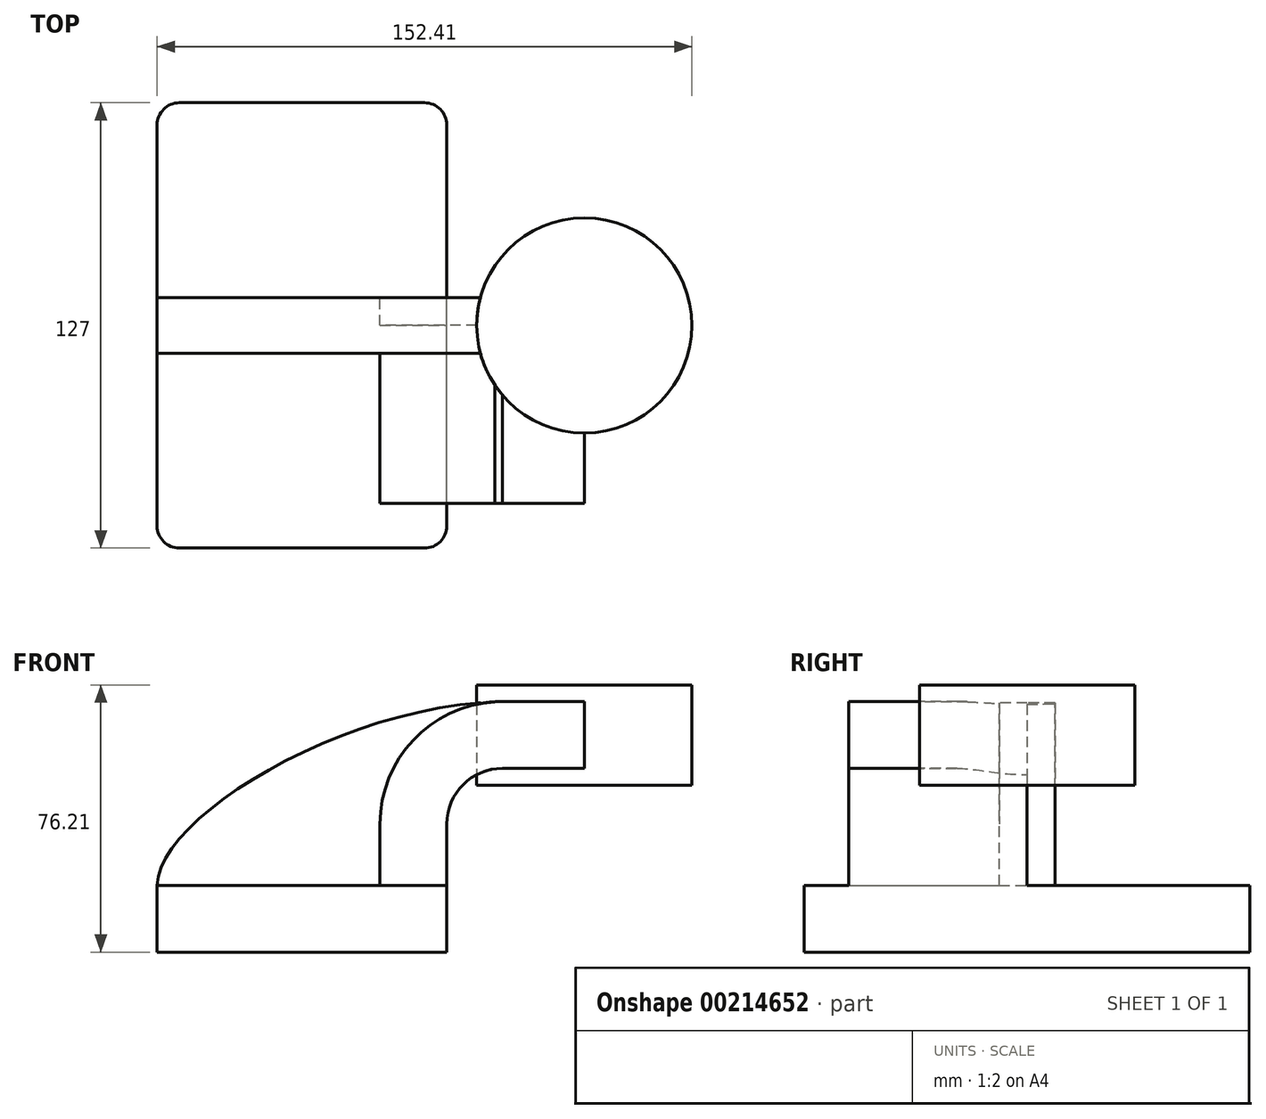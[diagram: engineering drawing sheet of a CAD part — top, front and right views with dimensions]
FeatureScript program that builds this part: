
annotation { "Feature Type Name" : "Feature", "Feature Type Description" : "" }
export const myFeature = defineFeature(function(context is Context, id is Id, definition is map)
    precondition{}
    {
        {
            var Q0;
            Q0=qCreatedBy(makeId("Front.planeOp"),FACE);
            var sketch = newSketch(context, id + "F0", { "sketchPlane" : qUnion([Q0])});
            skLineSegment(sketch, "E0.bottom", {"start": v(-41.28, -9.53) * mm, "end": v(41.28, -9.53) * mm});
            skLineSegment(sketch, "E0.top", {"start": v(-41.28, 9.53) * mm, "end": v(41.28, 9.53) * mm});
            skLineSegment(sketch, "E0.left", {"start": v(-41.28, -9.53) * mm, "end": v(-41.28, 9.53) * mm});
            skLineSegment(sketch, "E0.right", {"start": v(41.28, -9.53) * mm, "end": v(41.28, 9.53) * mm});
            skPoint(sketch, "E0.middle", {"position": v(0, 0) * mm});
            skLineSegment(sketch, "E1.bottom", {"start": v(60.32, 38.1) * mm, "end": v(111.12, 38.1) * mm});
            skLineSegment(sketch, "E1.top", {"start": v(60.32, 66.67) * mm, "end": v(111.12, 66.67) * mm});
            skLineSegment(sketch, "E1.left", {"start": v(60.32, 38.1) * mm, "end": v(60.32, 66.67) * mm});
            skLineSegment(sketch, "E1.right", {"start": v(111.12, 38.1) * mm, "end": v(111.12, 66.67) * mm});
            skPoint(sketch, "E1.middle", {"position": v(85.72, 52.39) * mm});
            skLineSegment(sketch, "E2", {"start": v(41.28, 9.53) * mm, "end": v(41.28, 27) * mm});
            skArc(sketch, "E3", {"start": v(41.27, 27) * mm, "mid": v(45.92, 38.23) * mm, "end": v(57.15, 42.88) * mm});
            skLineSegment(sketch, "E4", {"start": v(57.15, 42.88) * mm, "end": v(80.46, 42.88) * mm});
            skLineSegment(sketch, "E5.0", {"start": v(57.15, 61.93) * mm, "end": v(80.46, 61.93) * mm});
            skArc(sketch, "E5.1", {"start": v(22.22, 27) * mm, "mid": v(32.45, 51.7) * mm, "end": v(57.15, 61.93) * mm});
            skLineSegment(sketch, "E5.2", {"start": v(22.22, 9.53) * mm, "end": v(22.22, 27) * mm});
            skLineSegment(sketch, "E6", {"start": v(80.46, 38.1) * mm, "end": v(80.46, 66.67) * mm});
            skFitSpline(sketch, "E7", {"points": [v(-41.28, 9.52) * mm, v(57.15, 61.93) * mm], "startDerivative": vector(0.94, 57.52) * mm, "endDerivative": vector(138.38, 2.96) * mm});
            skSolve(sketch);
        }
        {
            var Q0;
            Q0=makeQuery(id+"F0.imprint","IMPRINT",FACE,{"disambiguationData":[TD([[makeQuery(id+"F0.imprint","IMPRINT",EDGE,{"derivedFrom":sQuery(id+"F0.wireOp",EDGE,"E0.bottom")}),1.0]])]});
            extrude(context, id + "F1", {"entities" : qUnion([Q0]), "endBound" : BoundingType.SYMMETRIC, "depth" : 127 * mm});
        }
        {
            var Q0;
            {var subQ1=sQuery(id+"F0.wireOp",EDGE,"E2");Q0=makeQuery(id+"F0.imprint","IMPRINT",FACE,{"disambiguationData":[TD([[makeQuery(id+"F0.imprint","IMPRINT",EDGE,{"derivedFrom":subQ1}),1.0]])]});}
            var Q1;
            {var subQ0=sQuery(id+"F0.wireOp",EDGE,"E4");var subQ1=sQuery(id+"F0.wireOp",EDGE,"E1.left");var subQ2=makeQuery(id+"F0.imprint","INTERSECT",VERTEX,{"derivedFrom":[subQ1,subQ0]});Q1=makeQuery(id+"F0.imprint","IMPRINT",FACE,{"disambiguationData":[TD([[makeQuery(id+"F0.imprint","IMPRINT",EDGE,{"disambiguationData":[TD([[subQ2,-1.0]])],"derivedFrom":subQ1}),-1.0]])]});}
            extrude(context, id + "F2", {"entities" : qUnion([Q0, Q1]), "operationType" : NewBodyOperationType.ADD, "depth" : 50.8 * mm});
        }
        {
            var Q0;
            {var subQ3=sQuery(id+"F0.wireOp",EDGE,"E5.2");Q0=makeQuery(id+"F0.imprint","IMPRINT",FACE,{"disambiguationData":[TD([[makeQuery(id+"F0.imprint","IMPRINT",EDGE,{"derivedFrom":subQ3}),1.0]])]});}
            extrude(context, id + "F3", {"entities" : qUnion([Q0]), "operationType" : NewBodyOperationType.ADD, "endBound" : BoundingType.SYMMETRIC, "depth" : 15.88 * mm});
        }
        {
            var Q0;
            {var subQ0=sQuery(id+"F0.wireOp",EDGE,"E1.right");Q0=makeQuery(id+"F0.imprint","IMPRINT",FACE,{"disambiguationData":[TD([[makeQuery(id+"F0.imprint","IMPRINT",EDGE,{"derivedFrom":subQ0}),1.0]])]});}
            var Q1;
            Q1=sQuery(id+"F0.wireOp",EDGE,"E6");
            revolve(context, id + "F4", {"operationType" : NewBodyOperationType.ADD, "entities" : qUnion([Q0]), "axis" : qUnion([Q1]), "revolveType" : RevolveType.FULL});
        }
        {
            var Q0;
            Q0=makeQuery(id+"F1.opExtrude","CAP_EDGE",EDGE,{"disambiguationData":[OSD([sQuery(id+"F0.wireOp",EDGE,"E0.right")])],"isStart":false});
            var Q1;
            Q1=makeQuery(id+"F1.opExtrude","CAP_EDGE",EDGE,{"disambiguationData":[OSD([sQuery(id+"F0.wireOp",EDGE,"E0.left")])],"isStart":false});
            var Q2;
            Q2=makeQuery(id+"F1.opExtrude","CAP_EDGE",EDGE,{"disambiguationData":[OSD([sQuery(id+"F0.wireOp",EDGE,"E0.right")])],"isStart":true});
            var Q3;
            Q3=makeQuery(id+"F1.opExtrude","CAP_EDGE",EDGE,{"disambiguationData":[OSD([sQuery(id+"F0.wireOp",EDGE,"E0.left")])],"isStart":true});
            fillet(context, id + "F5", {"entities" : qUnion([Q0, Q1, Q2, Q3]), "radius" : 6.35 * mm, "tangentPropagation" : true, "allowEdgeOverflow" : false});
        }
    });
